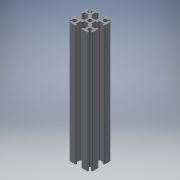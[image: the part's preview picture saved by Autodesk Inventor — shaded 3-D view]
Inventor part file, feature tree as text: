
AUTODESK INVENTOR PART (.ipt)
format: ipt  version: 2018.3 (Build 223284000, 284)  size: 992,768 bytes
history: native  units: mm
features: sketch x6, extrude x6, projected_geometry x6, plane x1, fillet x1
ambient origin geometry x8: Origin, YZ Plane, XZ Plane, XY Plane, X Axis, Y Axis, Z Axis, Center Point
bodies: Solid1 (feature_tree)
feature tree (20):
  sketch  "Sketch1"  dims[d0=10.0mm d1=0.0mm d2=165.1mm d3=0.0mm]
  plane  "Work Plane1"
  extrude  "Extrusion1"  Depth=165.1mm TaperAngle=0.0deg
  sketch  "Sketch2"  dims[d4=228.6mm d5=0.0mm d6=12.7mm d7=0.0mm]
  extrude  "Extrusion2"  Depth=12.7mm TaperAngle=0.0deg
  extrude  "Extrusion3"  Depth=5.0mm TaperAngle=0.0deg
  extrude  "Extrusion4"  [1 undecoded]
  extrude  "Extrusion5"  [1 undecoded]
  extrude  "Extrusion6"  [1 undecoded]
  projected_geometry  "Projected Loop1"
  projected_geometry  "Projected Loop2"
  sketch  "Sketch3"  dims[d8=10.0mm d9=0.0mm d10=5.0mm d11=0.0mm]
  projected_geometry  "Projected Loop3"
  sketch  "Sketch4"
  projected_geometry  "Projected Loop4"
  sketch  "Sketch5"
  projected_geometry  "Projected Loop5"
  sketch  "Sketch6"
  projected_geometry  "Projected Loop6"
  fillet  "Fillet6"  [1 undecoded]
note: 4 required parameter values undecoded (feature->parameter linkage not recoverable at this tier; creation-order binding heuristic only, values carry confidence <= 0.55)
